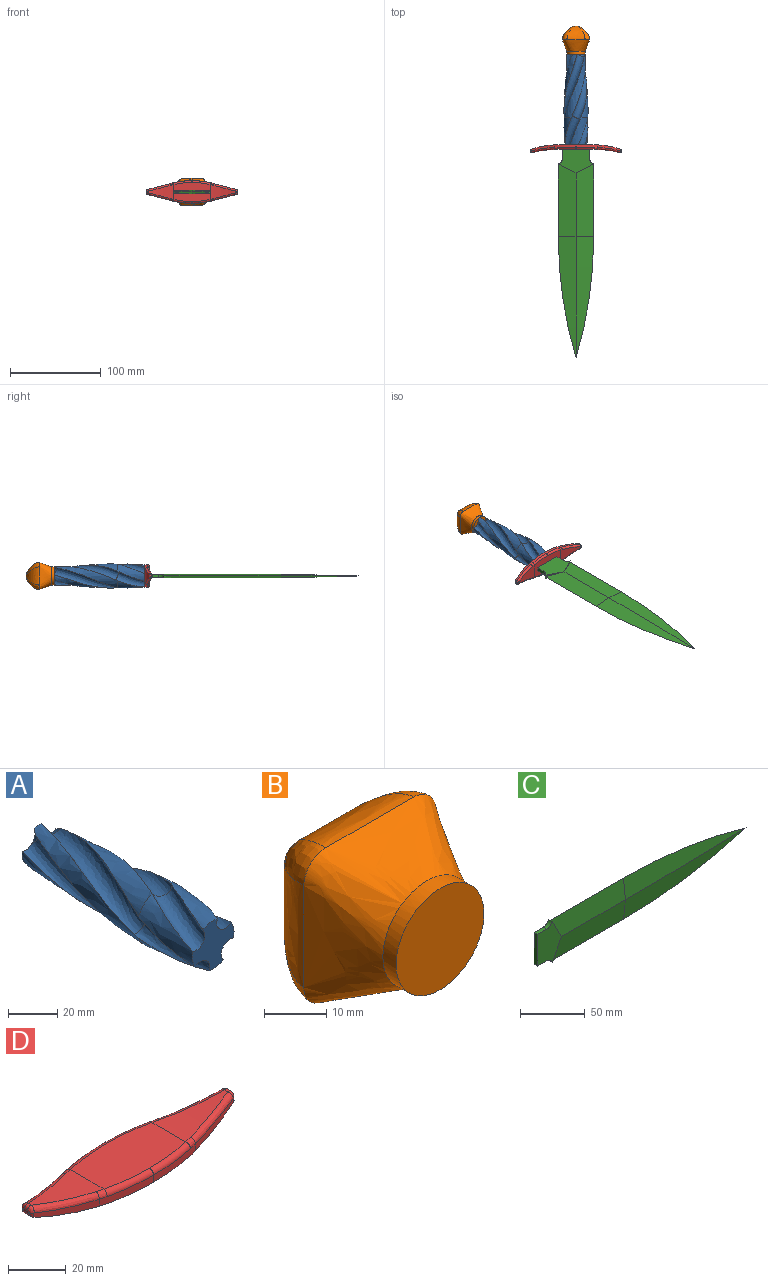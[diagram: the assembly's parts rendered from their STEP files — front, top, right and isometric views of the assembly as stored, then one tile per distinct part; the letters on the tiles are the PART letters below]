
ASSEMBLY  parts=4 mates=3
PART A: 22 faces, bbox 45.4x104.4x40.1 mm
  f0: plane 24x24mm, normal (0,-1,0), area 309.3mm2, adj f5,f6,f7,f9,f12,f15,f18,f21
  f1: plane 21.4x21.4mm, normal (0,1,0), area 158.7mm2, adj f2,f3,f4,f8,f10,f11,f13,f14
  f2: cone r=14mm half-angle=3.3deg, axis (0,-1,0), area 586.7mm2, adj f1,f5,f11,f12,f19,f20
  f3: cone r=14mm half-angle=3.3deg, axis (0,-1,0), area 586.7mm2, adj f1,f6,f16,f17,f20,f21
  f4: cone r=14mm half-angle=3.3deg, axis (0,-1,0), area 586.7mm2, adj f1,f7,f13,f14,f17,f18
  f5: cone r=12mm half-angle=3.8deg, axis (0,1,0), area 300.1mm2, adj f0,f2,f12,f20,f21
  f6: cone r=12mm half-angle=3.8deg, axis (0,1,0), area 300.1mm2, adj f0,f3,f17,f18,f21
  f7: cone r=12mm half-angle=3.8deg, axis (0,1,0), area 300.1mm2, adj f0,f4,f14,f15,f18
  f8: cone r=14mm half-angle=3.3deg, axis (0,-1,0), area 586.7mm2, adj f1,f9,f10,f11,f14,f15
  f9: cone r=12mm half-angle=3.8deg, axis (0,1,0), area 300.1mm2, adj f0,f8,f11,f12,f15
  f10: cylinder r=5mm len=7.94mm, axis (-0.46,-0.78,0.42), area 14.9mm2, adj f1,f8,f11
  f11: bspline ~75.51x28.97mm, area 949.4mm2, adj f1,f2,f8,f9,f10,f12
  f12: bspline ~35.82x27.24mm, area 426.3mm2, adj f0,f2,f5,f9,f11
  f13: cylinder r=5mm len=7.94mm, axis (0.42,-0.78,0.46), area 14.9mm2, adj f1,f4,f14
  f14: bspline ~75.51x29.02mm, area 925.9mm2, adj f1,f4,f7,f8,f13,f15
  f15: bspline ~32.29x20.01mm, area 425.2mm2, adj f0,f7,f8,f9,f14
  f16: cylinder r=5mm len=7.94mm, axis (0.46,-0.78,-0.42), area 14.9mm2, adj f1,f3,f17
  f17: bspline ~75.52x28.97mm, area 949.4mm2, adj f1,f3,f4,f6,f16,f18
  f18: bspline ~32.3x20mm, area 426.3mm2, adj f0,f4,f6,f7,f17
  f19: cylinder r=5mm len=7.94mm, axis (-0.42,-0.78,-0.46), area 14.9mm2, adj f1,f2,f20
  f20: bspline ~75.52x29.02mm, area 926mm2, adj f1,f2,f3,f5,f19,f21
  f21: bspline ~35.6x31.03mm, area 425mm2, adj f0,f3,f5,f6,f20
PART B: 11 faces, bbox 30x31x30 mm
  f0: cylinder r=10mm len=20mm, axis (0,1,0), area 188.5mm2, adj f1,f2
  f1: plane 20x20mm, normal (0,-1,0), area 314.2mm2, adj f0
  f2: bspline ~30x30mm, area 1264mm2, adj f0,f3,f4,f5,f6,f7,f8,f9
  f3: bspline ~15x15mm, area 114mm2, adj f2,f4,f5
  f4: bspline ~20x15mm, area 273.9mm2, adj f2,f3,f6
  f5: bspline ~20x15mm, area 273.3mm2, adj f2,f3,f7
  f6: bspline ~15x15mm, area 114mm2, adj f2,f4,f8
  f7: bspline ~15x15mm, area 114mm2, adj f2,f5,f9
  f8: bspline ~20x15mm, area 273.9mm2, adj f2,f6,f10
  f9: bspline ~20x15mm, area 273.9mm2, adj f2,f7,f10
  f10: bspline ~15x15mm, area 114mm2, adj f2,f8,f9
PART C: 19 faces, bbox 230x4x39 mm
  f0: plane 80x19.5mm, normal (0,0.99,0.1), area 1470.2mm2, adj f1,f2,f3,f10
  f1: plane 80x19.5mm, normal (0,0.99,-0.1), area 1470.2mm2, adj f0,f4,f5,f8
  f2: plane 80x19.5mm, normal (0,-0.99,0.1), area 1470.2mm2, adj f0,f5,f6,f9
  f3: cone r=450.66mm half-angle=84.1deg, axis (0,-1,0), area 1758.5mm2, adj f0,f4,f6
  f4: cone r=470.16mm half-angle=84.1deg, axis (0,-1,0), area 1758.5mm2, adj f1,f3,f7
  f5: plane 80x19.5mm, normal (0,-0.99,-0.1), area 1470.2mm2, adj f1,f2,f7,f14
  f6: cone r=470.16mm half-angle=84.1deg, axis (0,1,0), area 1758.5mm2, adj f2,f3,f7
  f7: cone r=450.66mm half-angle=84.1deg, axis (0,1,0), area 1758.5mm2, adj f4,f5,f6
  f8: plane 19.5x10mm, normal (0.89,0,-0.46), area 21.9mm2, adj f1,f13,f18
  f9: plane 19.5x10mm, normal (0.89,0,0.46), area 21.9mm2, adj f2,f15,f17
  f10: plane 19.5x10mm, normal (0.89,0,0.46), area 21.9mm2, adj f0,f15,f18
  f11: plane 30x4mm, normal (-1,0,0), area 120mm2, adj f12,f16,f17,f18
  f12: plane 10x4mm, normal (0,0,-1), area 40mm2, adj f11,f13,f17,f18
  f13: cylinder r=6.25mm len=6mm, axis (0,1,0), area 32.2mm2, adj f8,f12,f14,f17,f18
  f14: plane 19.5x10mm, normal (0.89,0,-0.46), area 21.9mm2, adj f5,f13,f17
  f15: cylinder r=6.25mm len=6mm, axis (0,1,0), area 32.2mm2, adj f9,f10,f16,f17,f18
  f16: plane 10x4mm, normal (0,0,1), area 40mm2, adj f11,f15,f17,f18
  f17: plane 39x26mm, normal (0,-1,0), area 689.2mm2, adj f9,f11,f12,f13,f14,f15,f16
  f18: plane 39x26mm, normal (0,1,0), area 689.2mm2, adj f8,f10,f11,f12,f13,f15,f16
PART D: 44 faces, bbox 100.1x26.2x9.1 mm
  f0: plane 2.69x0.98mm, normal (-1,0,0), area 2.5mm2, adj f18,f19,f20,f21,f26,f43
  f1: plane 2.69x0.98mm, normal (1,0,0), area 2.5mm2, adj f22,f23,f24,f25,f34,f35
  f2: cylinder r=92.5mm len=28.97mm, axis (0,1,0), area 387.2mm2, adj f3,f12,f13,f15,f17,f18,f20,f21
  f3: plane 40x25mm, normal (0,0,-1), area 942.2mm2, adj f2,f4,f8,f9,f14,f15,f16,f17
  f4: cylinder r=92.5mm len=28.97mm, axis (0,1,0), area 387.2mm2, adj f3,f10,f11,f14,f16,f22,f24,f25
  f5: cylinder r=114.5mm len=28.13mm, axis (0,1,0), area 258.8mm2, adj f6,f23,f32,f33,f36,f37
  f6: plane 40x21mm, normal (0,0,1), area 780.9mm2, adj f5,f7,f29,f30,f31,f38,f39,f40
  f7: cylinder r=114.5mm len=28.13mm, axis (0,1,0), area 258.8mm2, adj f6,f19,f27,f28,f41,f42
  f8: plane 3x0.07mm, normal (0,-1,0), area 0.2mm2, adj f3,f16,f17,f39
  f9: plane 3x0.07mm, normal (0,1,0), area 0.2mm2, adj f3,f14,f15,f30
  f10: plane 25.39x6.75mm, normal (0.25,-0.97,0), area 67.1mm2, adj f4,f16,f25,f36
  f11: plane 25.39x6.75mm, normal (0.25,0.97,0), area 67.1mm2, adj f4,f14,f22,f33
  f12: plane 25.39x6.75mm, normal (-0.25,0.97,0), area 67.1mm2, adj f2,f15,f21,f27
  f13: plane 25.39x6.75mm, normal (-0.25,-0.97,0), area 67.1mm2, adj f2,f17,f18,f42
  f14: cylinder r=92.5mm len=23.54mm, axis (0,0,-1), area 71.3mm2, adj f3,f4,f9,f11,f31,f32
  f15: cylinder r=92.5mm len=23.54mm, axis (0,0,-1), area 71.3mm2, adj f2,f3,f9,f12,f28,f29
  f16: cylinder r=92.5mm len=23.54mm, axis (0,0,1), area 71.3mm2, adj f3,f4,f8,f10,f37,f38
  f17: cylinder r=92.5mm len=23.54mm, axis (0,0,1), area 71.3mm2, adj f2,f3,f8,f13,f40,f41
  f18: cylinder r=1.5mm len=1.88mm, axis (0,0,-1), area 2.5mm2, adj f0,f2,f13,f20,f43
  f19: cylinder r=1.5mm len=1.87mm, axis (0,1,0), area 4.3mm2, adj f0,f7,f26,f43
  f20: cylinder r=1.5mm len=5.54mm, axis (0,1,0), area 7.7mm2, adj f0,f2,f18,f21
  f21: cylinder r=1.5mm len=1.88mm, axis (0,0,-1), area 2.5mm2, adj f0,f2,f12,f20,f26
  f22: cylinder r=1.5mm len=1.88mm, axis (0,0,1), area 2.5mm2, adj f1,f4,f11,f24,f34
  f23: cylinder r=1.5mm len=1.87mm, axis (0,1,0), area 4.3mm2, adj f1,f5,f34,f35
  f24: cylinder r=1.5mm len=5.54mm, axis (0,1,0), area 7.7mm2, adj f1,f4,f22,f25
  f25: cylinder r=1.5mm len=1.88mm, axis (0,0,1), area 2.5mm2, adj f1,f4,f10,f24,f35
  f26: bspline ~2.92x2.55mm, area 5.5mm2, adj f0,f19,f21,f27
  f27: bspline ~26.12x8.66mm, area 84.5mm2, adj f7,f12,f26,f28
  f28: bspline ~15.87x5.73mm, area 10mm2, adj f7,f15,f27,f29
  f29: torus R=90.5mm, axis (0,0,1), area 64.1mm2, adj f6,f15,f28,f30
  f30: cylinder r=2mm len=2mm, axis (-1,0,0), area 0.2mm2, adj f6,f9,f29,f31
  f31: torus R=90.5mm, axis (0,0,1), area 64.1mm2, adj f6,f14,f30,f32
  f32: bspline ~15.87x5.73mm, area 10mm2, adj f5,f14,f31,f33
  f33: bspline ~26.12x8.66mm, area 84.5mm2, adj f5,f11,f32,f34
  f34: bspline ~2.73x2.48mm, area 5.5mm2, adj f1,f22,f23,f33
  f35: bspline ~2.89x2.28mm, area 5.5mm2, adj f1,f23,f25,f36
  f36: bspline ~26.12x8.66mm, area 84.5mm2, adj f5,f10,f35,f37
  f37: bspline ~15.87x5.73mm, area 10mm2, adj f5,f16,f36,f38
  f38: torus R=90.5mm, axis (0,0,1), area 64.1mm2, adj f6,f16,f37,f39
  f39: cylinder r=2mm len=2mm, axis (1,0,0), area 0.2mm2, adj f6,f8,f38,f40
  f40: torus R=90.5mm, axis (0,0,1), area 64.1mm2, adj f6,f17,f39,f41
  f41: bspline ~15.87x5.73mm, area 10mm2, adj f7,f17,f40,f42
  f42: bspline ~26.12x8.66mm, area 84.5mm2, adj f7,f13,f41,f43
  f43: bspline ~2.63x2.53mm, area 5.5mm2, adj f0,f18,f19,f42
PLACE A t=(66.34,20.99,-9.85)mm
PLACE B t=(66.34,93.99,-9.85)mm
PLACE C rot(axis=(-0.58,0.58,-0.58),120deg) t=(51.34,-14.01,-11.85)mm
PLACE D rot(axis=(1,0,0),90deg) t=(46.34,-9.01,2.65)mm
MATE fastened C.f11 <-> D.f6  axis (0,1,0) through (66.34,-14.01,-9.85)mm
MATE fastened B.f0 <-> A.f2  axis (0,-1,0) through (66.34,90.99,-9.85)mm
MATE fastened D.f3 <-> A.f2  axis (0,1,0) through (66.34,-9.01,-9.85)mm
